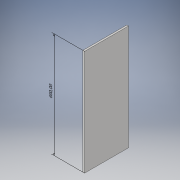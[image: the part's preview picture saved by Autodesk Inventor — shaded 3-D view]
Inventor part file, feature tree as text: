
AUTODESK INVENTOR PART (.ipt)
format: ipt  version: 2019 (Build 230136000, 136)  size: 102,912 bytes
history: native  units: mm
features: other x2, extrude x1, sketch x1
ambient origin geometry x8: Origin, YZ Plane, XZ Plane, XY Plane, X Axis, Y Axis, Z Axis, Center Point
bodies: Solid1 (feature_tree)
feature tree (4):
  other  "Annotations"
  extrude  "Extrusion1"  Depth=150.0mm
  sketch  "Sketch4"  dims[d3=600.0mm d5=150.0mm d9=250.0mm d10=125.0mm d11=10.0mm d12=0.0mm d13=0.0mm d14=10.0mm d15=600.0mm]
  other  "Linear Dimension 1"
